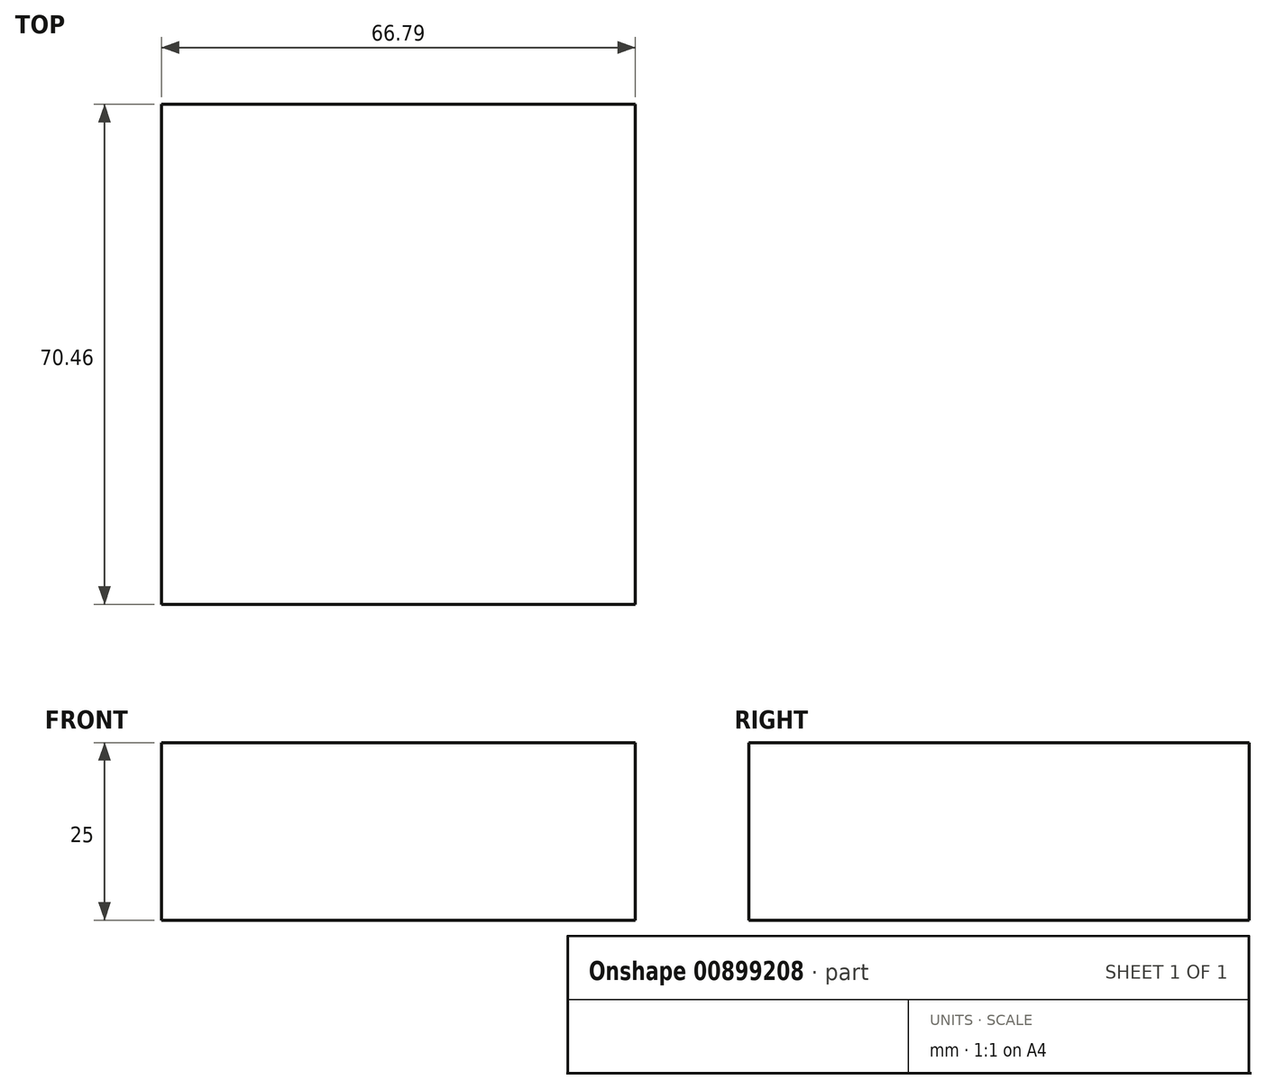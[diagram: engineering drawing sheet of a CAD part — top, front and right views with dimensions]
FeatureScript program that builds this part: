
annotation { "Feature Type Name" : "Feature", "Feature Type Description" : "" }
export const myFeature = defineFeature(function(context is Context, id is Id, definition is map)
    precondition{}
    {
        {
            var Q0;
            Q0=qCreatedBy(makeId("Top.planeOp"),FACE);
            var sketch = newSketch(context, id + "F0", { "sketchPlane" : qUnion([Q0])});
            skLineSegment(sketch, "E0.bottom", {"start": v(0, 0) * mm, "end": v(66.8, 0) * mm});
            skLineSegment(sketch, "E0.top", {"start": v(0, -70.46) * mm, "end": v(66.8, -70.46) * mm});
            skLineSegment(sketch, "E0.left", {"start": v(0, 0) * mm, "end": v(0, -70.46) * mm});
            skLineSegment(sketch, "E0.right", {"start": v(66.8, 0) * mm, "end": v(66.8, -70.46) * mm});
            skSolve(sketch);
        }
        {
            var Q0;
            Q0 = qSketchRegion(id + "F0", true);
            extrude(context, id + "F1", {"entities" : qUnion([Q0]), "depth" : 25 * mm, "offsetDistance" : 25 * mm});
        }
    });
